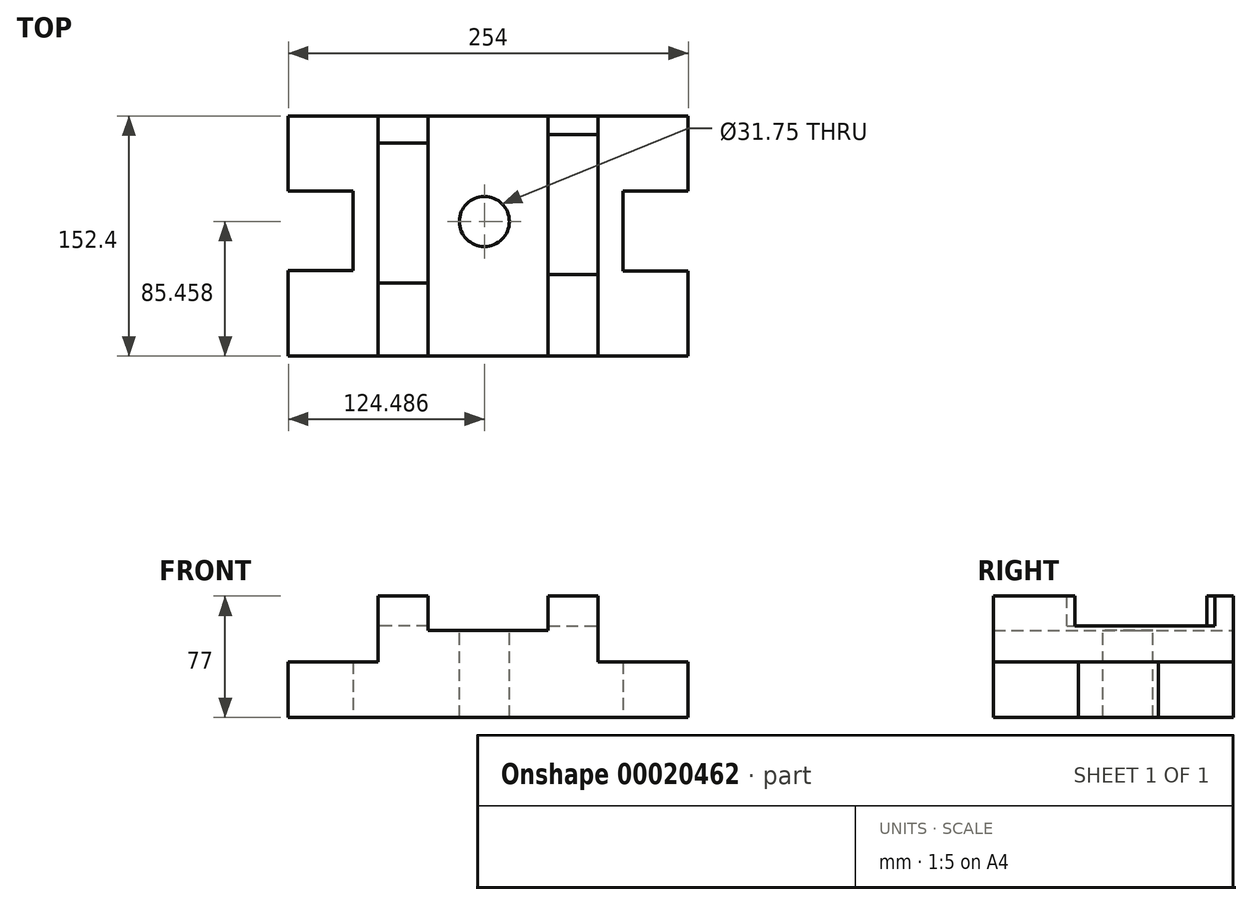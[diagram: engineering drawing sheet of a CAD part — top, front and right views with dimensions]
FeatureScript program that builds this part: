
annotation { "Feature Type Name" : "Feature", "Feature Type Description" : "" }
export const myFeature = defineFeature(function(context is Context, id is Id, definition is map)
    precondition{}
    {
        {
            var Q0;
            Q0=qCreatedBy(makeId("Front.planeOp"),FACE);
            var sketch = newSketch(context, id + "F0", { "sketchPlane" : qUnion([Q0])});
            skLineSegment(sketch, "E0.bottom", {"start": v(-17.65, 47.94) * mm, "end": v(14.1, 47.94) * mm});
            skLineSegment(sketch, "E0.top", {"start": v(-55.75, -29.06) * mm, "end": v(71.25, -29.06) * mm});
            skLineSegment(sketch, "E0.left", {"start": v(-55.75, 26.19) * mm, "end": v(-55.75, -29.06) * mm});
            skLineSegment(sketch, "E0.right", {"start": v(71.25, 6.18) * mm, "end": v(71.25, -29.06) * mm});
            skLineSegment(sketch, "E1.top", {"start": v(-55.75, 26.19) * mm, "end": v(-17.65, 26.19) * mm});
            skLineSegment(sketch, "E1.right", {"start": v(-17.65, 47.94) * mm, "end": v(-17.65, 26.19) * mm});
            skLineSegment(sketch, "E2.top", {"start": v(14.1, 6.18) * mm, "end": v(71.25, 6.18) * mm});
            skLineSegment(sketch, "E2.left", {"start": v(14.1, 47.94) * mm, "end": v(14.1, 6.18) * mm});
            skLineSegment(sketch, "E3.MirrorCS", {"start": v(-93.85, 47.94) * mm, "end": v(-125.6, 47.94) * mm});
            skLineSegment(sketch, "E4.MirrorCS", {"start": v(-182.75, 6.18) * mm, "end": v(-182.75, -29.06) * mm});
            skLineSegment(sketch, "E5.MirrorCS", {"start": v(-55.75, -29.06) * mm, "end": v(-182.75, -29.06) * mm});
            skLineSegment(sketch, "E6.MirrorCS", {"start": v(-125.6, 47.94) * mm, "end": v(-125.6, 6.18) * mm});
            skLineSegment(sketch, "E7.MirrorCS", {"start": v(-125.6, 6.18) * mm, "end": v(-182.75, 6.18) * mm});
            skLineSegment(sketch, "E8.MirrorCS", {"start": v(-55.75, 26.19) * mm, "end": v(-93.85, 26.19) * mm});
            skLineSegment(sketch, "E9.MirrorCS", {"start": v(-93.85, 47.94) * mm, "end": v(-93.85, 26.19) * mm});
            skSolve(sketch);
        }
        {
            var Q0;
            Q0 = qSketchRegion(id + "F0", true);
            extrude(context, id + "F1", {"entities" : qUnion([Q0]), "depth" : 152.4 * mm});
        }
        {
            var Q0;
            Q0=makeQuery(id+"F1.opExtrude","SWEPT_FACE",FACE,{"disambiguationData":[OSD([sQuery(id+"F0.wireOp",EDGE,"E0.right")])]});
            var sketch = newSketch(context, id + "F2", { "sketchPlane" : qUnion([Q0])});
            skLineSegment(sketch, "E10.bottom", {"start": v(-98.38, 6.18) * mm, "end": v(-47.58, 6.18) * mm});
            skLineSegment(sketch, "E10.top", {"start": v(-98.38, -29.06) * mm, "end": v(-47.58, -29.06) * mm});
            skLineSegment(sketch, "E10.left", {"start": v(-98.38, 6.18) * mm, "end": v(-98.38, -29.06) * mm});
            skLineSegment(sketch, "E10.right", {"start": v(-47.58, 6.18) * mm, "end": v(-47.58, -29.06) * mm});
            skSolve(sketch);
        }
        {
            var Q0;
            Q0 = qSketchRegion(id + "F2", true);
            extrude(context, id + "F3", {"entities" : qUnion([Q0]), "operationType" : NewBodyOperationType.REMOVE, "oppositeDirection" : true, "depth" : 41.27 * mm});
        }
        {
            var Q0;
            Q0=makeQuery(id+"F1.opExtrude","SWEPT_FACE",FACE,{"disambiguationData":[OSD([sQuery(id+"F0.wireOp",EDGE,"E0.bottom")])]});
            var sketch = newSketch(context, id + "F4", { "sketchPlane" : qUnion([Q0])});
            skLineSegment(sketch, "E11.bottom", {"start": v(-17.65, -100.6) * mm, "end": v(14.1, -100.6) * mm});
            skLineSegment(sketch, "E11.top", {"start": v(-17.65, -11.7) * mm, "end": v(14.1, -11.7) * mm});
            skLineSegment(sketch, "E11.left", {"start": v(-17.65, -100.6) * mm, "end": v(-17.65, -11.7) * mm});
            skLineSegment(sketch, "E11.right", {"start": v(14.1, -100.6) * mm, "end": v(14.1, -11.7) * mm});
            skLineSegment(sketch, "E12.left", {"start": v(14.1, -100.6) * mm, "end": v(14.1, -100.6) * mm});
            skLineSegment(sketch, "E12.right", {"start": v(14.1, -100.6) * mm, "end": v(14.1, -100.6) * mm});
            skSolve(sketch);
        }
        {
            var Q0;
            Q0 = qSketchRegion(id + "F4", true);
            extrude(context, id + "F5", {"entities" : qUnion([Q0]), "operationType" : NewBodyOperationType.REMOVE, "oppositeDirection" : true, "depth" : 19.05 * mm});
        }
        {
            var Q0;
            Q0=makeQuery(id+"F1.opExtrude","SWEPT_FACE",FACE,{"disambiguationData":[OSD([sQuery(id+"F0.wireOp",EDGE,"E4.MirrorCS")])]});
            var sketch = newSketch(context, id + "F6", { "sketchPlane" : qUnion([Q0])});
            skLineSegment(sketch, "E13.bottom", {"start": v(47.57, 6.18) * mm, "end": v(98.15, 6.18) * mm});
            skLineSegment(sketch, "E13.top", {"start": v(47.57, -29.06) * mm, "end": v(98.15, -29.06) * mm});
            skLineSegment(sketch, "E13.left", {"start": v(47.57, 6.18) * mm, "end": v(47.57, -29.06) * mm});
            skLineSegment(sketch, "E13.right", {"start": v(98.15, 6.18) * mm, "end": v(98.15, -29.06) * mm});
            skSolve(sketch);
        }
        {
            var Q0;
            Q0 = qSketchRegion(id + "F6", true);
            extrude(context, id + "F7", {"entities" : qUnion([Q0]), "operationType" : NewBodyOperationType.REMOVE, "oppositeDirection" : true, "depth" : 41.27 * mm});
        }
        {
            var Q0;
            Q0=makeQuery(id+"F1.opExtrude","SWEPT_FACE",FACE,{"disambiguationData":[OSD([sQuery(id+"F0.wireOp",EDGE,"E3.MirrorCS")])]});
            var sketch = newSketch(context, id + "F8", { "sketchPlane" : qUnion([Q0])});
            skLineSegment(sketch, "E14.bottom", {"start": v(-93.85, -16.98) * mm, "end": v(-125.6, -16.98) * mm});
            skLineSegment(sketch, "E14.top", {"start": v(-93.85, -105.88) * mm, "end": v(-125.6, -105.88) * mm});
            skLineSegment(sketch, "E14.left", {"start": v(-93.85, -16.98) * mm, "end": v(-93.85, -105.88) * mm});
            skLineSegment(sketch, "E14.right", {"start": v(-125.6, -16.98) * mm, "end": v(-125.6, -105.88) * mm});
            skSolve(sketch);
        }
        {
            var Q0;
            Q0 = qSketchRegion(id + "F8", true);
            extrude(context, id + "F9", {"entities" : qUnion([Q0]), "operationType" : NewBodyOperationType.REMOVE, "oppositeDirection" : true, "depth" : 19.05 * mm});
        }
        {
            var Q0;
            Q0=makeQuery(id+"F1.opExtrude","SWEPT_FACE",FACE,{"disambiguationData":[OSD([sQuery(id+"F0.wireOp",EDGE,"E1.top"),sQuery(id+"F0.wireOp",EDGE,"E8.MirrorCS")])]});
            var sketch = newSketch(context, id + "F10", { "sketchPlane" : qUnion([Q0])});
            skCircle(sketch, "E15", {"center": v(-58.26, -66.94) * mm, "radius": 15.88 * mm});
            skSolve(sketch);
        }
        {
            var Q0;
            Q0 = qSketchRegion(id + "F10", true);
            extrude(context, id + "F11", {"entities" : qUnion([Q0]), "operationType" : NewBodyOperationType.REMOVE, "endBound" : BoundingType.THROUGH_ALL, "oppositeDirection" : true, "depth" : 25.4 * mm});
        }
    });
